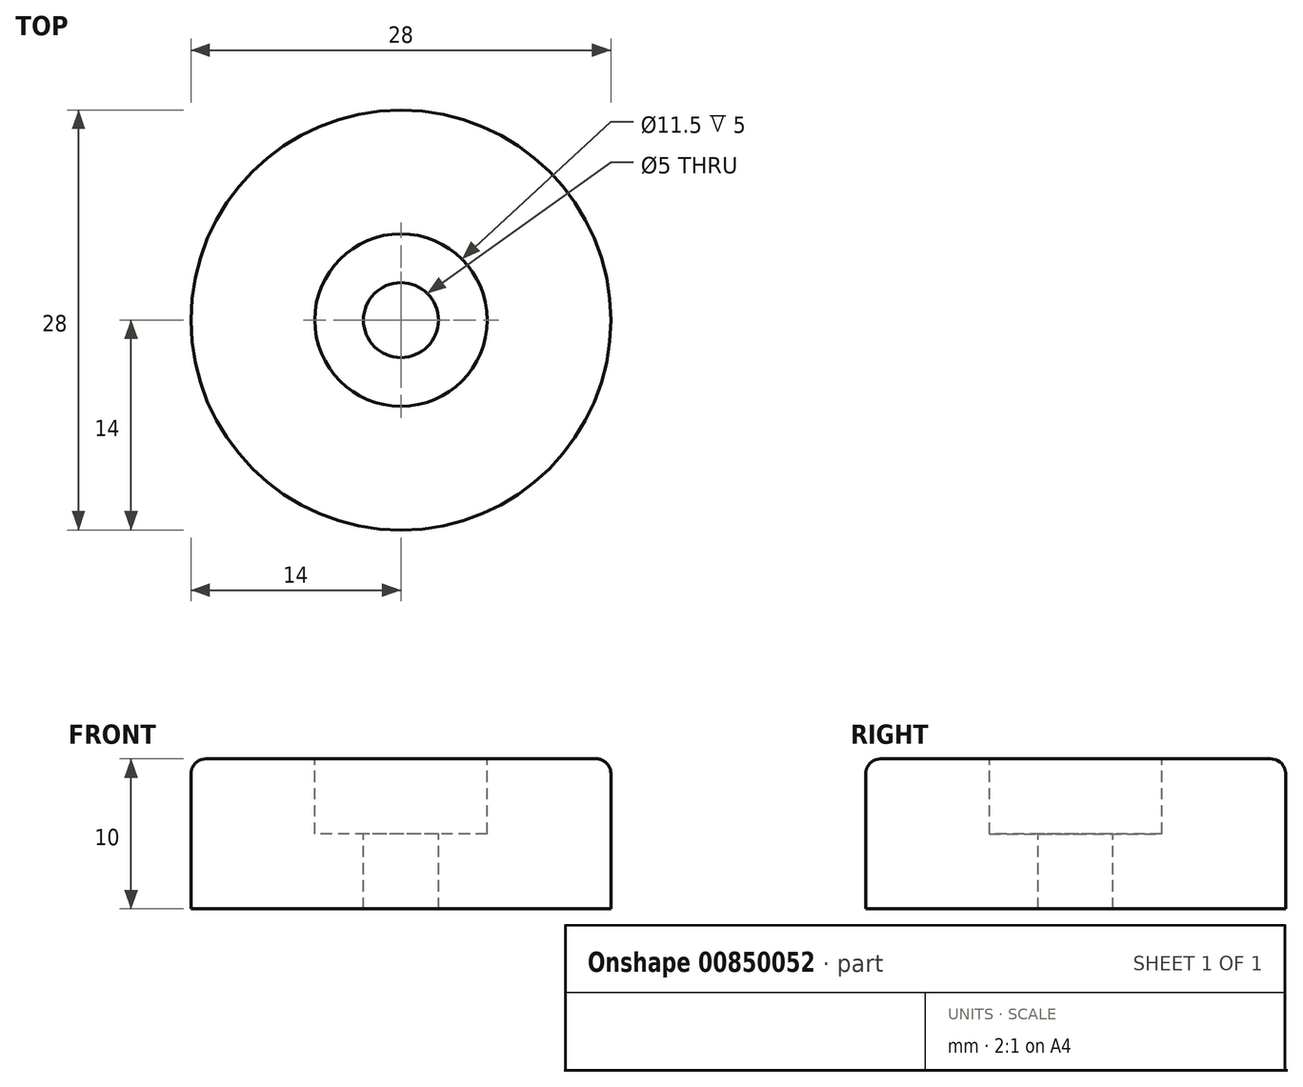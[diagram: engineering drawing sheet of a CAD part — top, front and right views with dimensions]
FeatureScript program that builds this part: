
annotation { "Feature Type Name" : "Feature", "Feature Type Description" : "" }
export const myFeature = defineFeature(function(context is Context, id is Id, definition is map)
    precondition{}
    {
        {
            var Q0;
            Q0=qCreatedBy(makeId("Top.planeOp"),FACE);
            var sketch = newSketch(context, id + "F0", { "sketchPlane" : qUnion([Q0])});
            skCircle(sketch, "E0", {"center": v(0, 0) * mm, "radius": 14 * mm});
            skSolve(sketch);
        }
        {
            var Q0;
            Q0 = qSketchRegion(id + "F0", true);
            extrude(context, id + "F1", {"entities" : qUnion([Q0]), "depth" : 10 * mm, "offsetDistance" : 25 * mm});
        }
        {
            var Q0;
            Q0=makeQuery(id+"F1.opExtrude","CAP_FACE",FACE,{"disambiguationData":[OSD([sQuery(id+"F0.wireOp",EDGE,"E0")])],"isStart":false});
            var sketch = newSketch(context, id + "F2", { "sketchPlane" : qUnion([Q0])});
            skCircle(sketch, "E1", {"center": v(0, 0) * mm, "radius": 5.75 * mm});
            skSolve(sketch);
        }
        {
            var Q0;
            Q0 = qSketchRegion(id + "F2", true);
            extrude(context, id + "F3", {"entities" : qUnion([Q0]), "operationType" : NewBodyOperationType.REMOVE, "oppositeDirection" : true, "depth" : 5 * mm, "offsetDistance" : 25 * mm});
        }
        {
            var Q0;
            Q0=makeQuery(id+"F3.boolean.opBoolean","COPY",FACE,{"derivedFrom":makeQuery(id+"F3.opExtrude","CAP_FACE",FACE,{"disambiguationData":[OSD([sQuery(id+"F2.wireOp",EDGE,"E1")])],"isStart":false})});
            var sketch = newSketch(context, id + "F4", { "sketchPlane" : qUnion([Q0])});
            skCircle(sketch, "E2", {"center": v(0, 0) * mm, "radius": 2.5 * mm});
            skSolve(sketch);
        }
        {
            var Q0;
            Q0 = qSketchRegion(id + "F4", true);
            extrude(context, id + "F5", {"entities" : qUnion([Q0]), "operationType" : NewBodyOperationType.REMOVE, "endBound" : BoundingType.THROUGH_ALL, "oppositeDirection" : true, "depth" : 25 * mm, "offsetDistance" : 25 * mm});
        }
        {
            var Q0;
            Q0=makeQuery(id+"F1.opExtrude","CAP_EDGE",EDGE,{"disambiguationData":[OSD([sQuery(id+"F0.wireOp",EDGE,"E0")])],"isStart":false});
            fillet(context, id + "F6", {"entities" : qUnion([Q0]), "radius" : 1 * mm, "tangentPropagation" : true, "allowEdgeOverflow" : false});
        }
    });
